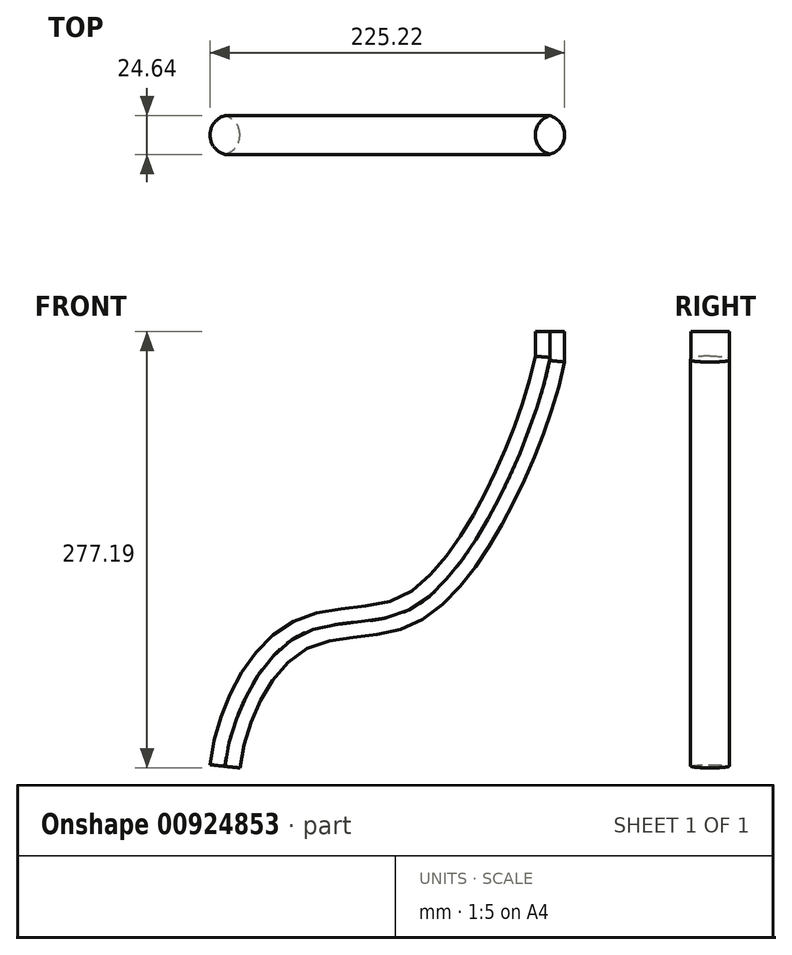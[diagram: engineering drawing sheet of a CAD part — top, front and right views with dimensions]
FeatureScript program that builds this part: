
annotation { "Feature Type Name" : "Feature", "Feature Type Description" : "" }
export const myFeature = defineFeature(function(context is Context, id is Id, definition is map)
    precondition{}
    {
        {
            var Q0;
            Q0=qCreatedBy(makeId("Front.planeOp"),FACE);
            var sketch = newSketch(context, id + "F0", { "sketchPlane" : qUnion([Q0])});
            skFitSpline(sketch, "E0", {"points": [v(87.76, 162.03) * mm, v(0, 0) * mm, v(-78.54, -21.3) * mm, v(-118.52, -95.8) * mm], "startDerivative": vector(-64.32, -323.36) * mm, "endDerivative": vector(-26.71, -251.13) * mm});
            skFitSpline(sketch, "E1.0", {"points": [v(69.07, 165.75) * mm, v(68.48, 162.75) * mm, v(66.98, 156.19) * mm, v(63.88, 145.01) * mm, v(60, 132.85) * mm, v(55.37, 120) * mm, v(50.1, 106.73) * mm, v(44.22, 93.32) * mm, v(37.83, 80.06) * mm, v(31, 67.2) * mm, v(23.8, 55.04) * mm, v(16.36, 43.84) * mm, v(10.05, 35.55) * mm, v(5.02, 29.68) * mm, v(1.28, 25.7) * mm, v(-2.39, 22.18) * mm, v(-5.35, 19.64) * mm, v(-7.65, 17.86) * mm, v(-9.05, 16.86) * mm, v(-10.15, 16.12) * mm, v(-11.22, 15.43) * mm, v(-12.57, 14.61) * mm, v(-14.2, 13.72) * mm, v(-16.37, 12.63) * mm, v(-19.11, 11.44) * mm, v(-22.5, 10.25) * mm, v(-27.18, 8.93) * mm, v(-33.4, 7.7) * mm, v(-41.51, 6.66) * mm, v(-48.81, 5.93) * mm, v(-54.98, 5.23) * mm, v(-59.77, 4.58) * mm, v(-64.71, 3.73) * mm, v(-69.81, 2.6) * mm, v(-75.04, 1.1) * mm, v(-79.47, -0.54) * mm, v(-83.03, -2.12) * mm, v(-85.25, -3.23) * mm, v(-87.02, -4.2) * mm, v(-88.34, -4.97) * mm, v(-89.65, -5.77) * mm, v(-91.35, -6.87) * mm, v(-93.42, -8.32) * mm, v(-96.6, -10.75) * mm, v(-100.34, -14.02) * mm, v(-104.5, -18.22) * mm, v(-109.62, -24.15) * mm, v(-115.34, -32.08) * mm, v(-121.23, -42.16) * mm, v(-126.23, -52.6) * mm, v(-130.38, -63.17) * mm, v(-133.67, -73.68) * mm, v(-136.1, -83.96) * mm, v(-137.12, -90.56) * mm, v(-137.46, -93.8) * mm]});
            skLineSegment(sketch, "E2", {"start": v(-137.46, -93.8) * mm, "end": v(-118.52, -95.8) * mm});
            skLineSegment(sketch, "E3", {"start": v(69.07, 165.75) * mm, "end": v(69.07, 181.38) * mm});
            skLineSegment(sketch, "E4", {"start": v(69.07, 181.38) * mm, "end": v(87.76, 181.38) * mm});
            skLineSegment(sketch, "E5", {"start": v(87.76, 181.38) * mm, "end": v(87.76, 162.03) * mm});
            skSolve(sketch);
        }
        {
            var Q0;
            Q0 = qSketchRegion(id + "F0", true);
            extrude(context, id + "F1", {"entities" : qUnion([Q0]), "depth" : 25.4 * mm, "offsetDistance" : 25.4 * mm});
        }
        {
            var Q0;
            Q0=makeQuery(id+"F1.opExtrude","CAP_EDGE",EDGE,{"disambiguationData":[OSD([sQuery(id+"F0.wireOp",EDGE,"E1.0")])],"isStart":false});
            var Q1;
            Q1=makeQuery(id+"F1.opExtrude","CAP_EDGE",EDGE,{"disambiguationData":[OSD([sQuery(id+"F0.wireOp",EDGE,"E1.0")])],"isStart":true});
            var Q2;
            Q2=makeQuery(id+"F1.opExtrude","CAP_EDGE",EDGE,{"disambiguationData":[OSD([sQuery(id+"F0.wireOp",EDGE,"E0")])],"isStart":true});
            var Q3;
            Q3=makeQuery(id+"F1.opExtrude","CAP_EDGE",EDGE,{"disambiguationData":[OSD([sQuery(id+"F0.wireOp",EDGE,"E0")])],"isStart":false});
            var Q4;
            Q4=makeQuery(id+"F1.opExtrude","CAP_EDGE",EDGE,{"disambiguationData":[OSD([sQuery(id+"F0.wireOp",EDGE,"E5")])],"isStart":false});
            var Q5;
            Q5=makeQuery(id+"F1.opExtrude","CAP_EDGE",EDGE,{"disambiguationData":[OSD([sQuery(id+"F0.wireOp",EDGE,"E3")])],"isStart":false});
            var Q6;
            Q6=makeQuery(id+"F1.opExtrude","CAP_EDGE",EDGE,{"disambiguationData":[OSD([sQuery(id+"F0.wireOp",EDGE,"E5")])],"isStart":true});
            var Q7;
            Q7=makeQuery(id+"F1.opExtrude","CAP_EDGE",EDGE,{"disambiguationData":[OSD([sQuery(id+"F0.wireOp",EDGE,"E3")])],"isStart":true});
            fillet(context, id + "F2", {"entities" : qUnion([Q0, Q1, Q2, Q3, Q4, Q5, Q6, Q7]), "radius" : 12.7 * mm, "tangentPropagation" : true, "allowEdgeOverflow" : false});
        }
    });
